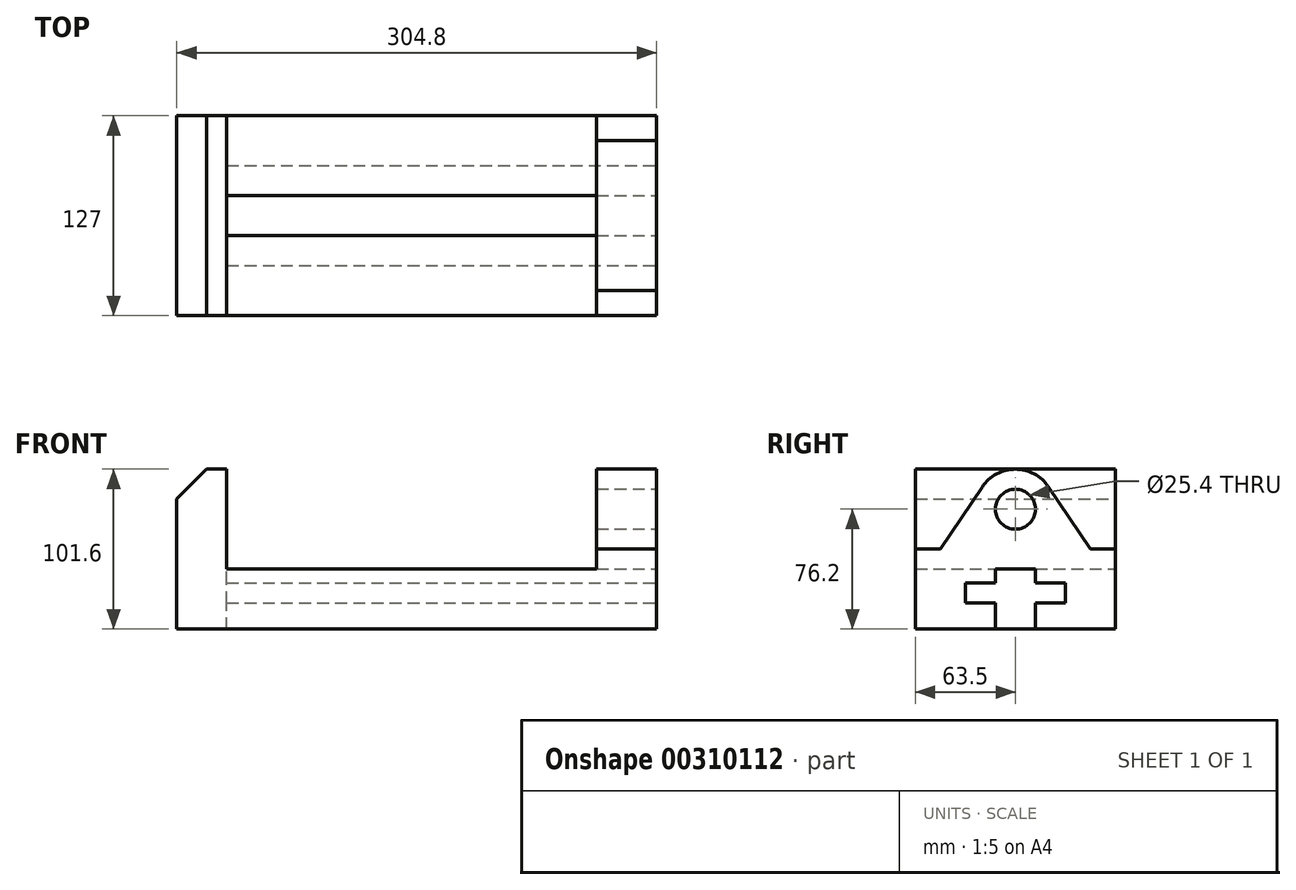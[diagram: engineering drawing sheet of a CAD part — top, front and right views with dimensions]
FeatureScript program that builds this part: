
annotation { "Feature Type Name" : "Feature", "Feature Type Description" : "" }
export const myFeature = defineFeature(function(context is Context, id is Id, definition is map)
    precondition{}
    {
        {
            var Q0;
            Q0=qCreatedBy(makeId("Front.planeOp"),FACE);
            var sketch = newSketch(context, id + "F0", { "sketchPlane" : qUnion([Q0])});
            skLineSegment(sketch, "E0.bottom", {"start": v(0, 0) * mm, "end": v(304.8, 0) * mm});
            skLineSegment(sketch, "E0.top", {"start": v(19.05, 101.6) * mm, "end": v(31.75, 101.6) * mm});
            skLineSegment(sketch, "E0.left", {"start": v(0, 0) * mm, "end": v(0, 82.55) * mm});
            skLineSegment(sketch, "E0.right", {"start": v(304.8, 0) * mm, "end": v(304.8, 101.6) * mm});
            skLineSegment(sketch, "E1", {"start": v(0, 82.55) * mm, "end": v(19.05, 101.6) * mm});
            skPoint(sketch, "E2.orphan", {"position": v(0, 101.6) * mm});
            skLineSegment(sketch, "E3.top", {"start": v(31.75, 38.1) * mm, "end": v(266.7, 38.1) * mm});
            skLineSegment(sketch, "E3.left", {"start": v(31.75, 101.6) * mm, "end": v(31.75, 38.1) * mm});
            skLineSegment(sketch, "E3.right", {"start": v(266.7, 101.6) * mm, "end": v(266.7, 38.1) * mm});
            skLineSegment(sketch, "E4.trimOffspring", {"start": v(266.7, 101.6) * mm, "end": v(304.8, 101.6) * mm});
            skSolve(sketch);
        }
        {
            var Q0;
            Q0 = qSketchRegion(id + "F0", true);
            extrude(context, id + "F1", {"entities" : qUnion([Q0]), "endBound" : BoundingType.SYMMETRIC, "depth" : 127 * mm});
        }
        {
            var Q0;
            Q0=makeQuery(id+"F1.opExtrude","SWEPT_FACE",FACE,{"disambiguationData":[OSD([sQuery(id+"F0.wireOp",EDGE,"E0.right")])]});
            var sketch = newSketch(context, id + "F2", { "sketchPlane" : qUnion([Q0])});
            skLineSegment(sketch, "E5", {"start": v(0, 38.1) * mm, "end": v(0, 104.86) * mm, "construction": true});
            skPoint(sketch, "E5.endSnap0", {"position": v(0, 101.6) * mm});
            skLineSegment(sketch, "E6", {"start": v(0, 0) * mm, "end": v(12.7, 0) * mm});
            skLineSegment(sketch, "E7", {"start": v(12.7, 0) * mm, "end": v(12.7, 16.51) * mm});
            skLineSegment(sketch, "E8", {"start": v(12.7, 16.51) * mm, "end": v(31.75, 16.51) * mm});
            skLineSegment(sketch, "E9", {"start": v(31.75, 16.51) * mm, "end": v(31.75, 29.21) * mm});
            skLineSegment(sketch, "E10", {"start": v(31.75, 29.21) * mm, "end": v(12.7, 29.21) * mm});
            skLineSegment(sketch, "E11", {"start": v(12.7, 29.21) * mm, "end": v(12.7, 38.1) * mm});
            skLineSegment(sketch, "E12", {"start": v(12.7, 38.1) * mm, "end": v(0, 38.1) * mm});
            skLineSegment(sketch, "E13", {"start": v(0, 38.1) * mm, "end": v(0, 0) * mm});
            skLineSegment(sketch, "E14.MirrorCS", {"start": v(-12.7, 16.51) * mm, "end": v(-31.75, 16.51) * mm});
            skLineSegment(sketch, "E15.MirrorCS", {"start": v(-31.75, 16.51) * mm, "end": v(-31.75, 29.21) * mm});
            skLineSegment(sketch, "E16.MirrorCS", {"start": v(-31.75, 29.21) * mm, "end": v(-12.7, 29.21) * mm});
            skLineSegment(sketch, "E17.MirrorCS", {"start": v(-12.7, 29.21) * mm, "end": v(-12.7, 38.1) * mm});
            skLineSegment(sketch, "E18.MirrorCS", {"start": v(-12.7, 0) * mm, "end": v(-12.7, 16.51) * mm});
            skLineSegment(sketch, "E19.MirrorCS", {"start": v(0, 0) * mm, "end": v(-12.7, 0) * mm});
            skLineSegment(sketch, "E20.MirrorCS", {"start": v(-12.7, 38.1) * mm, "end": v(0, 38.1) * mm});
            skSolve(sketch);
        }
        {
            var Q0;
            Q0 = qSketchRegion(id + "F2", true);
            extrude(context, id + "F3", {"entities" : qUnion([Q0]), "operationType" : NewBodyOperationType.REMOVE, "oppositeDirection" : true, "depth" : 273.05 * mm});
        }
        {
            var Q0;
            Q0=makeQuery(id+"F1.opExtrude","SWEPT_FACE",FACE,{"disambiguationData":[OSD([sQuery(id+"F0.wireOp",EDGE,"E0.right")])]});
            var sketch = newSketch(context, id + "F4", { "sketchPlane" : qUnion([Q0])});
            skLineSegment(sketch, "E21", {"start": v(-63.5, 50.8) * mm, "end": v(-47.63, 50.8) * mm});
            skLineSegment(sketch, "E22", {"start": v(63.5, 50.8) * mm, "end": v(47.63, 50.8) * mm});
            skLineSegment(sketch, "E23", {"start": v(-47.63, 50.8) * mm, "end": v(-21.1, 90.35) * mm});
            skLineSegment(sketch, "E24", {"start": v(47.63, 50.8) * mm, "end": v(21.1, 90.35) * mm});
            skArc(sketch, "E25", {"start": v(21.1, 90.35) * mm, "mid": v(0, 101.6) * mm, "end": v(-21.1, 90.35) * mm});
            skLineSegment(sketch, "E26", {"start": v(-63.5, 50.8) * mm, "end": v(-63.5, 101.6) * mm});
            skLineSegment(sketch, "E27", {"start": v(-63.5, 101.6) * mm, "end": v(0, 101.6) * mm});
            skLineSegment(sketch, "E28", {"start": v(0, 101.6) * mm, "end": v(63.5, 101.6) * mm});
            skLineSegment(sketch, "E29", {"start": v(63.5, 101.6) * mm, "end": v(63.5, 50.8) * mm});
            skSolve(sketch);
        }
        {
            var Q0;
            Q0 = qSketchRegion(id + "F4", true);
            extrude(context, id + "F5", {"entities" : qUnion([Q0]), "operationType" : NewBodyOperationType.REMOVE, "oppositeDirection" : true, "depth" : 38.1 * mm});
        }
        {
            var Q0;
            Q0=makeQuery(id+"F1.opExtrude","SWEPT_FACE",FACE,{"disambiguationData":[OSD([sQuery(id+"F0.wireOp",EDGE,"E0.right")])]});
            var sketch = newSketch(context, id + "F6", { "sketchPlane" : qUnion([Q0])});
            skCircle(sketch, "E30", {"center": v(0, 76.2) * mm, "radius": 12.7 * mm});
            skSolve(sketch);
        }
        {
            var Q0;
            Q0 = qSketchRegion(id + "F6", true);
            extrude(context, id + "F7", {"entities" : qUnion([Q0]), "operationType" : NewBodyOperationType.REMOVE, "oppositeDirection" : true, "depth" : 38.1 * mm});
        }
    });
